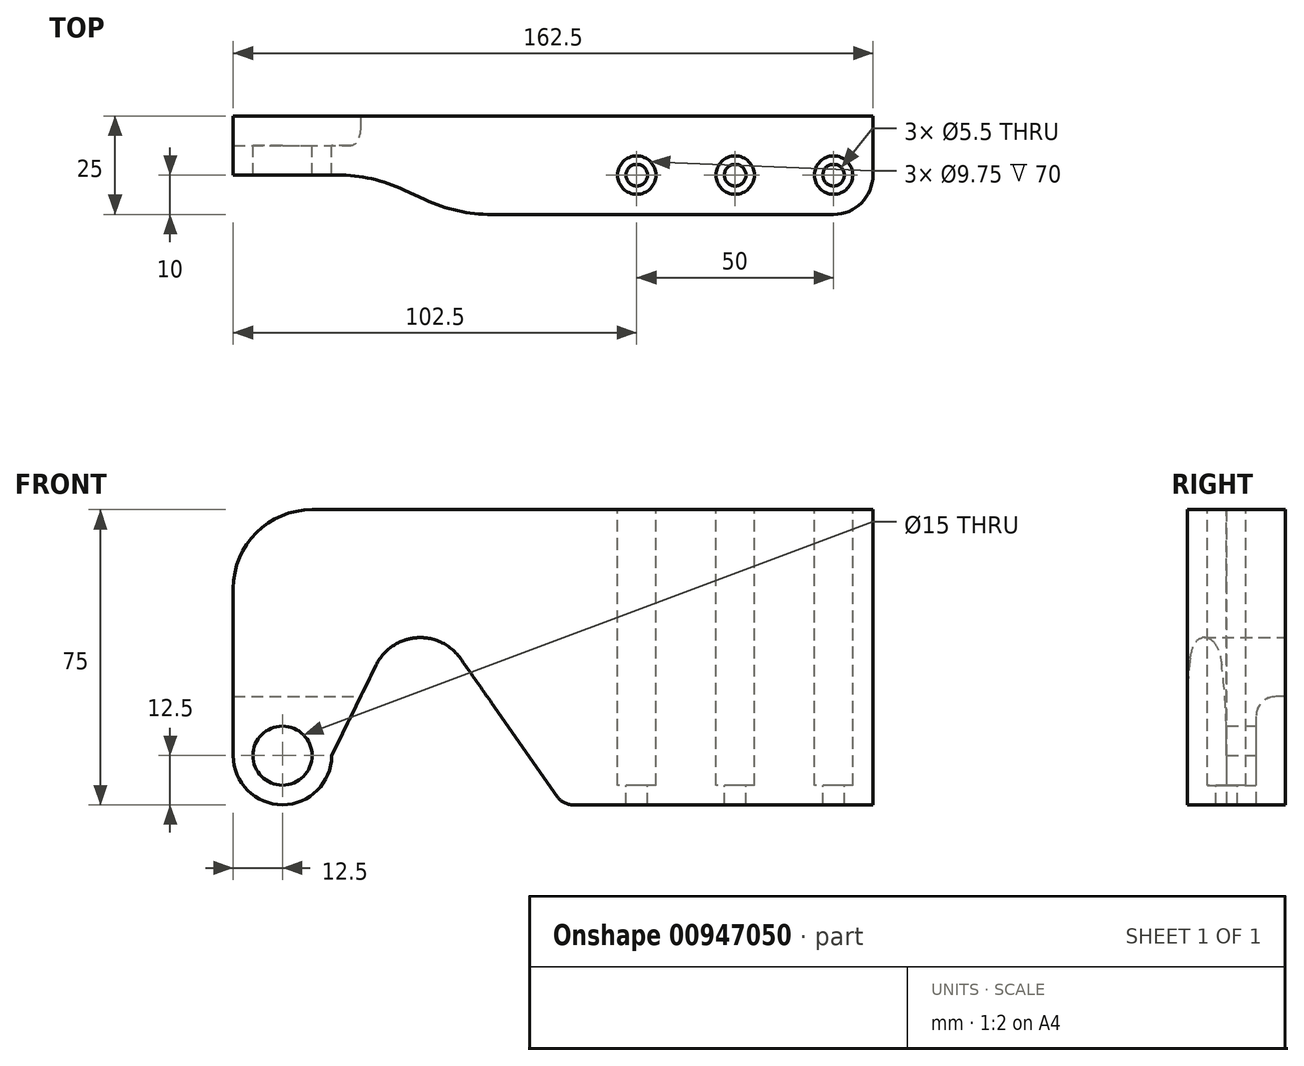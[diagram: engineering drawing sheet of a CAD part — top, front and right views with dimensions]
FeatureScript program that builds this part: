
annotation { "Feature Type Name" : "Feature", "Feature Type Description" : "" }
export const myFeature = defineFeature(function(context is Context, id is Id, definition is map)
    precondition{}
    {
        {
            var Q0;
            Q0=qCreatedBy(makeId("Front.planeOp"),FACE);
            var sketch = newSketch(context, id + "F0", { "sketchPlane" : qUnion([Q0])});
            skCircle(sketch, "E0", {"center": v(0, 0) * mm, "radius": 7.5 * mm});
            skLineSegment(sketch, "E1", {"start": v(71.27, -12.5) * mm, "end": v(150, -12.5) * mm});
            skLineSegment(sketch, "E2", {"start": v(150, -12.5) * mm, "end": v(150, 62.5) * mm});
            skLineSegment(sketch, "E3", {"start": v(150, 62.5) * mm, "end": v(-12.5, 62.5) * mm});
            skLineSegment(sketch, "E4", {"start": v(-12.5, 62.5) * mm, "end": v(-12.5, 0) * mm});
            skArc(sketch, "E5.filletArc", {"start": v(-12.5, 0) * mm, "mid": v(0, -12.5) * mm, "end": v(12.5, 0) * mm});
            skArc(sketch, "E6", {"start": v(45.24, 24.67) * mm, "mid": v(34.03, 29.96) * mm, "end": v(23.78, 23) * mm});
            skLineSegment(sketch, "E7", {"start": v(23.78, 23) * mm, "end": v(12.5, 0) * mm});
            skLineSegment(sketch, "E8", {"start": v(45.24, 24.67) * mm, "end": v(71.27, -12.5) * mm});
            skLineSegment(sketch, "E9", {"start": v(-67.57, 30) * mm, "end": v(159.6, 30) * mm, "construction": true});
            skLineSegment(sketch, "E10", {"start": v(35, 103.49) * mm, "end": v(35, -64.01) * mm, "construction": true});
            skSolve(sketch);
        }
        {
            var Q0;
            Q0=makeQuery(id+"F0.imprint","IMPRINT",FACE,{"disambiguationData":[TD([[makeQuery(id+"F0.imprint","IMPRINT",EDGE,{"derivedFrom":sQuery(id+"F0.wireOp",EDGE,"E0")}),-1.0]])]});
            extrude(context, id + "F1", {"entities" : qUnion([Q0]), "depth" : 25 * mm, "offsetDistance" : 25 * mm});
        }
        {
            var Q0;
            Q0=qCreatedBy(makeId("Right.planeOp"),FACE);
            var sketch = newSketch(context, id + "F2", { "sketchPlane" : qUnion([Q0])});
            skLineSegment(sketch, "E11.bottom", {"start": v(0, 15) * mm, "end": v(-7.5, 15) * mm});
            skLineSegment(sketch, "E11.top", {"start": v(0, -30) * mm, "end": v(-7.5, -30) * mm});
            skLineSegment(sketch, "E11.left", {"start": v(0, 15) * mm, "end": v(0, -30) * mm});
            skLineSegment(sketch, "E11.right", {"start": v(-7.5, 15) * mm, "end": v(-7.5, -30) * mm});
            skSolve(sketch);
        }
        {
            var Q0;
            Q0=makeQuery(id+"F2.imprint","IMPRINT",FACE,{"disambiguationData":[TD([[makeQuery(id+"F2.imprint","IMPRINT",EDGE,{"derivedFrom":sQuery(id+"F2.wireOp",EDGE,"E11.bottom")}),1.0]])]});
            extrude(context, id + "F3", {"entities" : qUnion([Q0]), "operationType" : NewBodyOperationType.REMOVE, "endBound" : BoundingType.SYMMETRIC, "oppositeDirection" : true, "depth" : 50 * mm, "offsetDistance" : 25 * mm});
        }
        {
            var Q0;
            Q0=makeQuery(id+"F1.opExtrude","SWEPT_FACE",FACE,{"disambiguationData":[OSD([sQuery(id+"F0.wireOp",EDGE,"E3")])]});
            var sketch = newSketch(context, id + "F4", { "sketchPlane" : qUnion([Q0])});
            skLineSegment(sketch, "E12", {"start": v(-67.5, -15) * mm, "end": v(182.31, -15) * mm, "construction": true});
            skPoint(sketch, "E13", {"position": v(140, -15) * mm});
            skPoint(sketch, "E14", {"position": v(115, -15) * mm});
            skPoint(sketch, "E15", {"position": v(90, -15) * mm});
            skSolve(sketch);
        }
        {
            var Q0;
            Q0=sQuery(id+"F4.wireOp",VERTEX,"E13");
            var Q1;
            Q1=sQuery(id+"F4.wireOp",VERTEX,"E14");
            var Q2;
            Q2=sQuery(id+"F4.wireOp",VERTEX,"E15");
            var Q3;
            Q3=makeQuery(id+"F1.opExtrude","SWEPT_BODY",BODY,{"disambiguationData":[OSD([sQuery(id+"F0.wireOp",EDGE,"E0"),sQuery(id+"F0.wireOp",EDGE,"E1"),sQuery(id+"F0.wireOp",EDGE,"E2"),sQuery(id+"F0.wireOp",EDGE,"E3"),sQuery(id+"F0.wireOp",EDGE,"E4"),sQuery(id+"F0.wireOp",EDGE,"E5.filletArc"),sQuery(id+"F0.wireOp",EDGE,"E6"),sQuery(id+"F0.wireOp",EDGE,"E7"),sQuery(id+"F0.wireOp",EDGE,"E8")])]});
            hole(context, id + "F5", {"style" : HoleStyle.C_BORE, "endStyle" : HoleEndStyle.THROUGH, "holeDiameter" : 5.5 * mm, "cBoreDiameter" : 9.75 * mm, "cBoreDepth" : 70 * mm, "majorDiameter" : 5 * mm, "isTappedThrough" : true, "tappedDepth" : 12 * mm, "tapClearance" : 3, "locations" : qUnion([Q0, Q1, Q2]), "scope" : qUnion([Q3])});
        }
        {
            var Q0;
            Q0=makeQuery(id+"F1.opExtrude","SWEPT_EDGE",EDGE,{"disambiguationData":[OSD([sQuery(id+"F0.wireOp",EDGE,"E3"),sQuery(id+"F0.wireOp",EDGE,"E4")])]});
            fillet(context, id + "F6", {"entities" : qUnion([Q0]), "radius" : 20 * mm, "tangentPropagation" : true, "allowEdgeOverflow" : false});
        }
        {
            var Q0;
            Q0=makeQuery(id+"F3.boolean.opBoolean","COPY",EDGE,{"derivedFrom":makeQuery(id+"F3.opExtrude","SWEPT_EDGE",EDGE,{"disambiguationData":[OSD([sQuery(id+"F2.wireOp",EDGE,"E11.bottom"),sQuery(id+"F2.wireOp",EDGE,"E11.right")])]})});
            fillet(context, id + "F7", {"entities" : qUnion([Q0]), "radius" : 5 * mm, "tangentPropagation" : true, "allowEdgeOverflow" : false});
        }
        {
            var Q0;
            Q0=makeQuery(id+"F1.opExtrude","CAP_EDGE",EDGE,{"disambiguationData":[OSD([sQuery(id+"F0.wireOp",EDGE,"E2")])],"isStart":false});
            fillet(context, id + "F8", {"entities" : qUnion([Q0]), "radius" : 10 * mm, "tangentPropagation" : true, "allowEdgeOverflow" : false});
        }
        {
            var Q0;
            Q0=makeQuery(id+"F1.opExtrude","SWEPT_EDGE",EDGE,{"disambiguationData":[OSD([sQuery(id+"F0.wireOp",EDGE,"E1"),sQuery(id+"F0.wireOp",EDGE,"E8")])]});
            fillet(context, id + "F9", {"entities" : qUnion([Q0]), "radius" : 5 * mm, "tangentPropagation" : true, "allowEdgeOverflow" : false});
        }
        {
            var Q0;
            Q0=qCreatedBy(makeId("Top.planeOp"),FACE);
            var sketch = newSketch(context, id + "F10", { "sketchPlane" : qUnion([Q0])});
            skLineSegment(sketch, "E16", {"start": v(-25, -15) * mm, "end": v(22.83, -15) * mm});
            skLineSegment(sketch, "E17", {"start": v(22.83, -15) * mm, "end": v(55, -30) * mm});
            skLineSegment(sketch, "E18", {"start": v(55, -30) * mm, "end": v(-25, -30) * mm});
            skLineSegment(sketch, "E19", {"start": v(-25, -30) * mm, "end": v(-25, -15) * mm});
            skSolve(sketch);
        }
        {
            var Q0;
            Q0=makeQuery(id+"F10.imprint","IMPRINT",FACE,{"disambiguationData":[TD([[makeQuery(id+"F10.imprint","IMPRINT",EDGE,{"derivedFrom":sQuery(id+"F10.wireOp",EDGE,"E16")}),-1.0]])]});
            extrude(context, id + "F11", {"entities" : qUnion([Q0]), "operationType" : NewBodyOperationType.REMOVE, "endBound" : BoundingType.SYMMETRIC, "depth" : 200 * mm, "offsetDistance" : 25 * mm});
        }
        {
            var Q0;
            Q0=makeQuery(id+"F11.boolean.opBoolean","COPY",EDGE,{"derivedFrom":makeQuery(id+"F11.opExtrude","SWEPT_EDGE",EDGE,{"disambiguationData":[OSD([sQuery(id+"F10.wireOp",EDGE,"E16"),sQuery(id+"F10.wireOp",EDGE,"E17")])]})});
            var Q1;
            Q1=makeQuery(id+"F11.boolean.opBoolean","INTERSECT",EDGE,{"derivedFrom":[makeQuery(id+"F1.opExtrude","CAP_FACE",FACE,{"disambiguationData":[OSD([sQuery(id+"F0.wireOp",EDGE,"E0"),sQuery(id+"F0.wireOp",EDGE,"E1"),sQuery(id+"F0.wireOp",EDGE,"E2"),sQuery(id+"F0.wireOp",EDGE,"E3"),sQuery(id+"F0.wireOp",EDGE,"E4"),sQuery(id+"F0.wireOp",EDGE,"E5.filletArc"),sQuery(id+"F0.wireOp",EDGE,"E6"),sQuery(id+"F0.wireOp",EDGE,"E7"),sQuery(id+"F0.wireOp",EDGE,"E8")])],"isStart":false}),makeQuery(id+"F11.opExtrude","SWEPT_FACE",FACE,{"disambiguationData":[OSD([sQuery(id+"F10.wireOp",EDGE,"E17")])]})]});
            fillet(context, id + "F12", {"entities" : qUnion([Q0, Q1]), "radius" : 40 * mm, "tangentPropagation" : true, "allowEdgeOverflow" : false});
        }
    });
